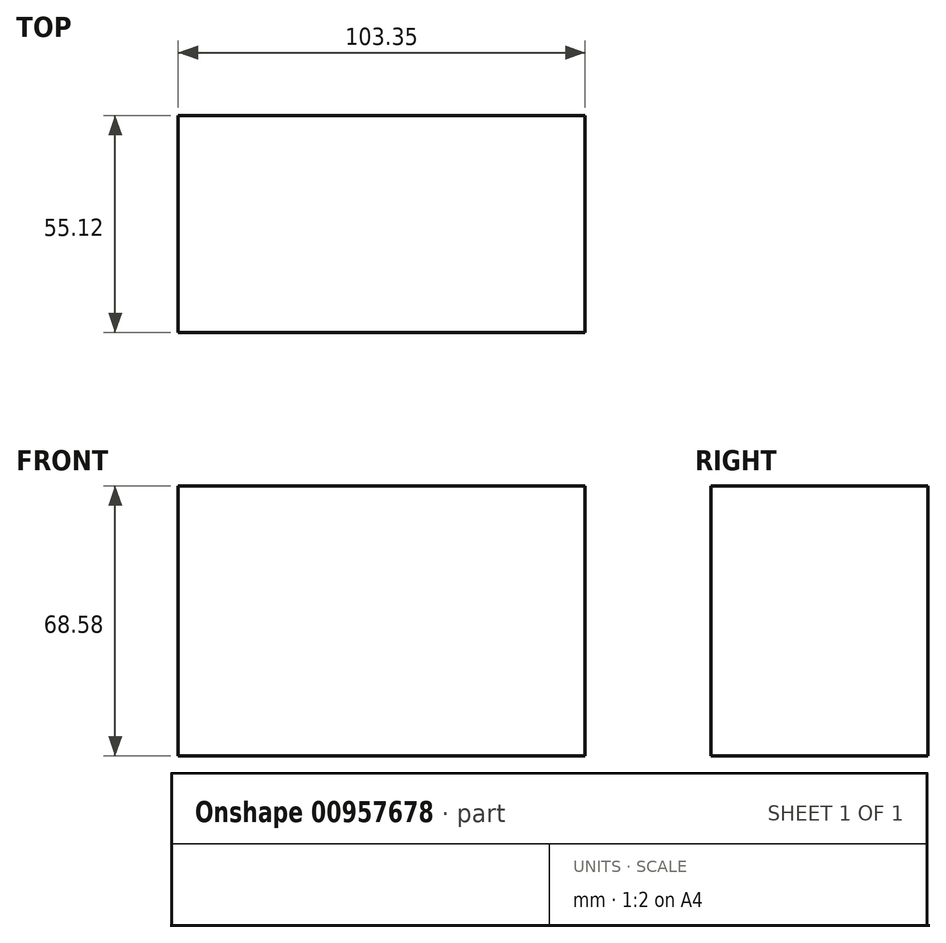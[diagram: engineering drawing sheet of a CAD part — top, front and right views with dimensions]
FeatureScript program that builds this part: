
annotation { "Feature Type Name" : "Feature", "Feature Type Description" : "" }
export const myFeature = defineFeature(function(context is Context, id is Id, definition is map)
    precondition{}
    {
        {
            var Q0;
            Q0=qCreatedBy(makeId("Top.planeOp"),FACE);
            var sketch = newSketch(context, id + "F0", { "sketchPlane" : qUnion([Q0])});
            skLineSegment(sketch, "E0.bottom", {"start": v(-44.67, -24.98) * mm, "end": v(58.68, -24.98) * mm});
            skLineSegment(sketch, "E0.top", {"start": v(-44.67, 30.14) * mm, "end": v(58.68, 30.14) * mm});
            skLineSegment(sketch, "E0.left", {"start": v(-44.67, -24.98) * mm, "end": v(-44.67, 30.14) * mm});
            skLineSegment(sketch, "E0.right", {"start": v(58.68, -24.98) * mm, "end": v(58.68, 30.14) * mm});
            skSolve(sketch);
        }
        {
            var Q0;
            Q0 = qSketchRegion(id + "F0", true);
            extrude(context, id + "F1", {"entities" : qUnion([Q0]), "depth" : 68.58 * mm, "offsetDistance" : 25.4 * mm});
        }
    });
